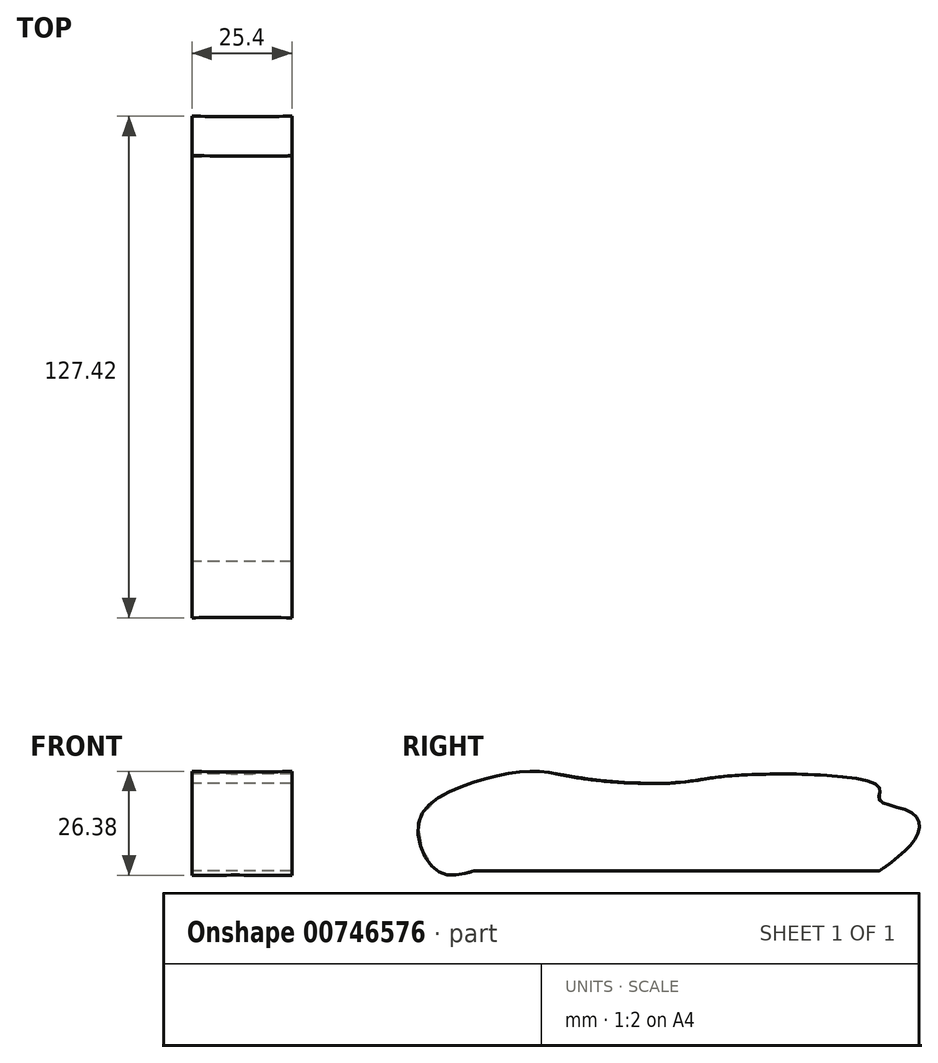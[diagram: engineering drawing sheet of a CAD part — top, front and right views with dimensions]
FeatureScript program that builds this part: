
annotation { "Feature Type Name" : "Feature", "Feature Type Description" : "" }
export const myFeature = defineFeature(function(context is Context, id is Id, definition is map)
    precondition{}
    {
        {
            var Q0;
            Q0=qCreatedBy(makeId("Right.planeOp"),FACE);
            cPlane(context, id + "F0", {"entities" : qUnion([Q0]), "cplaneType" : CPlaneType.OFFSET, "offset" : 25.4 * mm, "width" : 152.4 * mm, "height" : 152.4 * mm});
        }
        {
            var Q0;
            Q0=qCreatedBy(id+"F0.planeOp",FACE);
            var sketch = newSketch(context, id + "F1", { "sketchPlane" : qUnion([Q0])});
            skLineSegment(sketch, "E0", {"start": v(-49.56, -9.06) * mm, "end": v(53.37, -9.06) * mm});
            skFitSpline(sketch, "E1", {"points": [v(53.37, -9.06) * mm, v(63, -0.06) * mm, v(61.92, 5.56) * mm, v(53.37, 9.03) * mm, v(53.37, 12.24) * mm, v(16.48, 15.18) * mm, v(1.96, 13.31) * mm, v(-21.75, 14.38) * mm, v(-34.32, 16.25) * mm, v(-50.1, 13.31) * mm, v(-63.46, 3.95) * mm, v(-58.91, -9.06) * mm, v(-49.56, -9.06) * mm], "startDerivative": vector(147.84, 106.09) * mm, "endDerivative": vector(142.41, 39.85) * mm});
            skLineSegment(sketch, "E2", {"start": v(-28.18, 15.53) * mm, "end": v(-6.34, 29.64) * mm});
            skLineSegment(sketch, "E3", {"start": v(-6.34, 29.64) * mm, "end": v(15.43, 29.64) * mm});
            skLineSegment(sketch, "E4", {"start": v(15.43, 29.64) * mm, "end": v(40.04, 15.23) * mm});
            skSolve(sketch);
        }
        {
            var Q0;
            Q0=qCreatedBy(makeId("Right.planeOp"),FACE);
            var sketch = newSketch(context, id + "F2", { "sketchPlane" : qUnion([Q0])});
            skLineSegment(sketch, "E5", {"start": v(-49.56, -9.06) * mm, "end": v(53.37, -9.06) * mm});
            skFitSpline(sketch, "E6", {"points": [v(53.37, -9.06) * mm, v(63, -0.06) * mm, v(61.92, 5.56) * mm, v(53.37, 9.03) * mm, v(53.37, 12.24) * mm, v(16.48, 15.18) * mm, v(1.96, 13.31) * mm, v(-21.75, 14.38) * mm, v(-34.32, 16.25) * mm, v(-50.1, 13.31) * mm, v(-63.46, 3.95) * mm, v(-58.91, -9.06) * mm, v(-49.56, -9.06) * mm], "startDerivative": vector(147.84, 106.09) * mm, "endDerivative": vector(142.41, 39.85) * mm});
            skSolve(sketch);
        }
        {
            var Q0;
            Q0=makeQuery(id+"F1.imprint","IMPRINT",FACE,{"disambiguationData":[TD([[makeQuery(id+"F1.imprint","IMPRINT",EDGE,{"derivedFrom":sQuery(id+"F1.wireOp",EDGE,"E0")}),1.0]])]});
            var Q1;
            Q1=makeQuery(id+"F2.imprint","IMPRINT",FACE,{"disambiguationData":[TD([[makeQuery(id+"F2.imprint","IMPRINT",EDGE,{"derivedFrom":sQuery(id+"F2.wireOp",EDGE,"E5")}),1.0]])]});
            loft(context, id + "F3", {"sheetProfilesArray" : [{ "sheetProfileEntities" : qUnion([Q0]) }, { "sheetProfileEntities" : qUnion([Q1]) }]});
        }
    });
